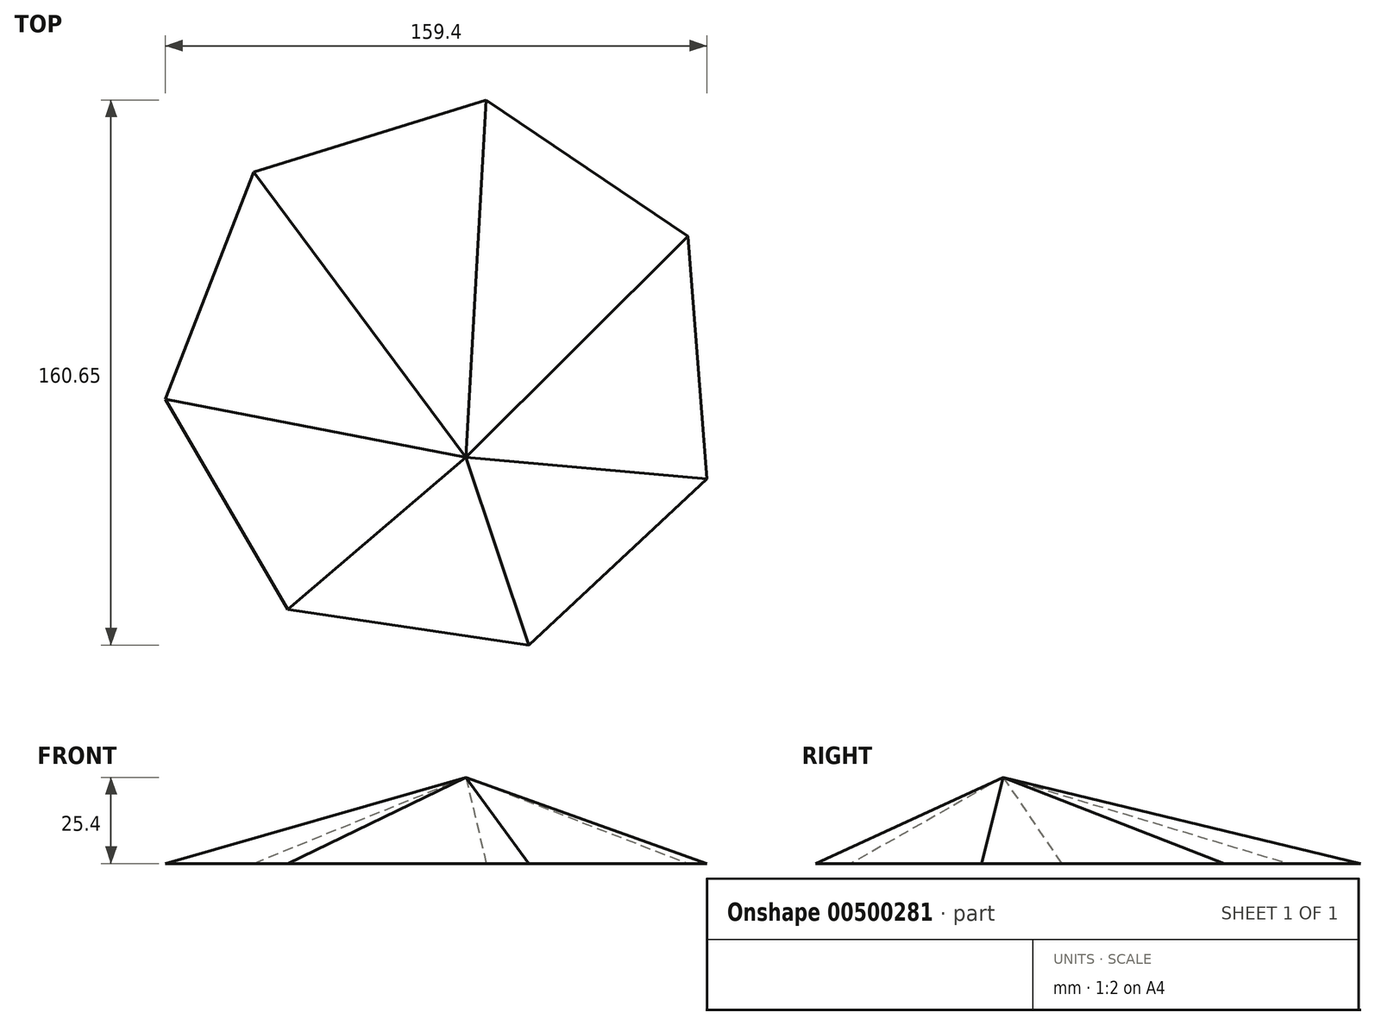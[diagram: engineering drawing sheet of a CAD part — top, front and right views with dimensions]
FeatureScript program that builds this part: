
annotation { "Feature Type Name" : "Feature", "Feature Type Description" : "" }
export const myFeature = defineFeature(function(context is Context, id is Id, definition is map)
    precondition{}
    {
        {
            var Q0;
            Q0=qCreatedBy(makeId("Top.planeOp"),FACE);
            var sketch = newSketch(context, id + "F0", { "sketchPlane" : qUnion([Q0])});
            skCircle(sketch, "E0.cCircle", {"center": v(0, 0) * mm, "radius": 82.64 * mm, "construction": true});
            skLineSegment(sketch, "E0.0", {"start": v(-56.37, 60.43) * mm, "end": v(12.1, 81.75) * mm});
            skLineSegment(sketch, "E0.1", {"start": v(12.1, 81.75) * mm, "end": v(71.46, 41.51) * mm});
            skLineSegment(sketch, "E0.2", {"start": v(71.46, 41.51) * mm, "end": v(77, -29.98) * mm});
            skLineSegment(sketch, "E0.3", {"start": v(77, -29.98) * mm, "end": v(24.57, -78.9) * mm});
            skLineSegment(sketch, "E0.4", {"start": v(24.57, -78.9) * mm, "end": v(-46.37, -68.4) * mm});
            skLineSegment(sketch, "E0.5", {"start": v(-46.37, -68.4) * mm, "end": v(-82.4, -6.4) * mm});
            skLineSegment(sketch, "E0.6", {"start": v(-82.4, -6.4) * mm, "end": v(-56.37, 60.43) * mm});
            skSolve(sketch);
        }
        {
            var Q0;
            Q0=qCreatedBy(makeId("Top.planeOp"),FACE);
            cPlane(context, id + "F1", {"entities" : qUnion([Q0]), "cplaneType" : CPlaneType.OFFSET, "offset" : 25.4 * mm, "width" : 152.4 * mm, "height" : 152.4 * mm});
        }
        {
            var Q0;
            Q0=qCreatedBy(id+"F1.planeOp",FACE);
            var sketch = newSketch(context, id + "F2", { "sketchPlane" : qUnion([Q0])});
            skLineSegment(sketch, "E1.bottom", {"start": v(-43.65, 24.03) * mm, "end": v(55.84, 24.03) * mm});
            skLineSegment(sketch, "E1.top", {"start": v(-43.65, -71.21) * mm, "end": v(55.84, -71.21) * mm});
            skLineSegment(sketch, "E1.left", {"start": v(-43.65, 24.03) * mm, "end": v(-43.65, -71.21) * mm});
            skLineSegment(sketch, "E1.right", {"start": v(55.84, 24.03) * mm, "end": v(55.84, -71.21) * mm});
            skPoint(sketch, "E1.middle", {"position": v(6.1, -23.6) * mm});
            skSolve(sketch);
        }
        {
            var Q0;
            Q0=sQuery(id+"F2.wireOp",VERTEX,"E1.middle");
            var Q1;
            Q1=makeQuery(id+"F0.imprint","IMPRINT",FACE,{"disambiguationData":[TD([[makeQuery(id+"F0.imprint","IMPRINT",EDGE,{"derivedFrom":sQuery(id+"F0.wireOp",EDGE,"E0.0")}),-1.0]])]});
            loft(context, id + "F3", {"sheetProfilesArray" : [{ "sheetProfileEntities" : qUnion([Q0]) }, { "sheetProfileEntities" : qUnion([Q1]) }]});
        }
    });
